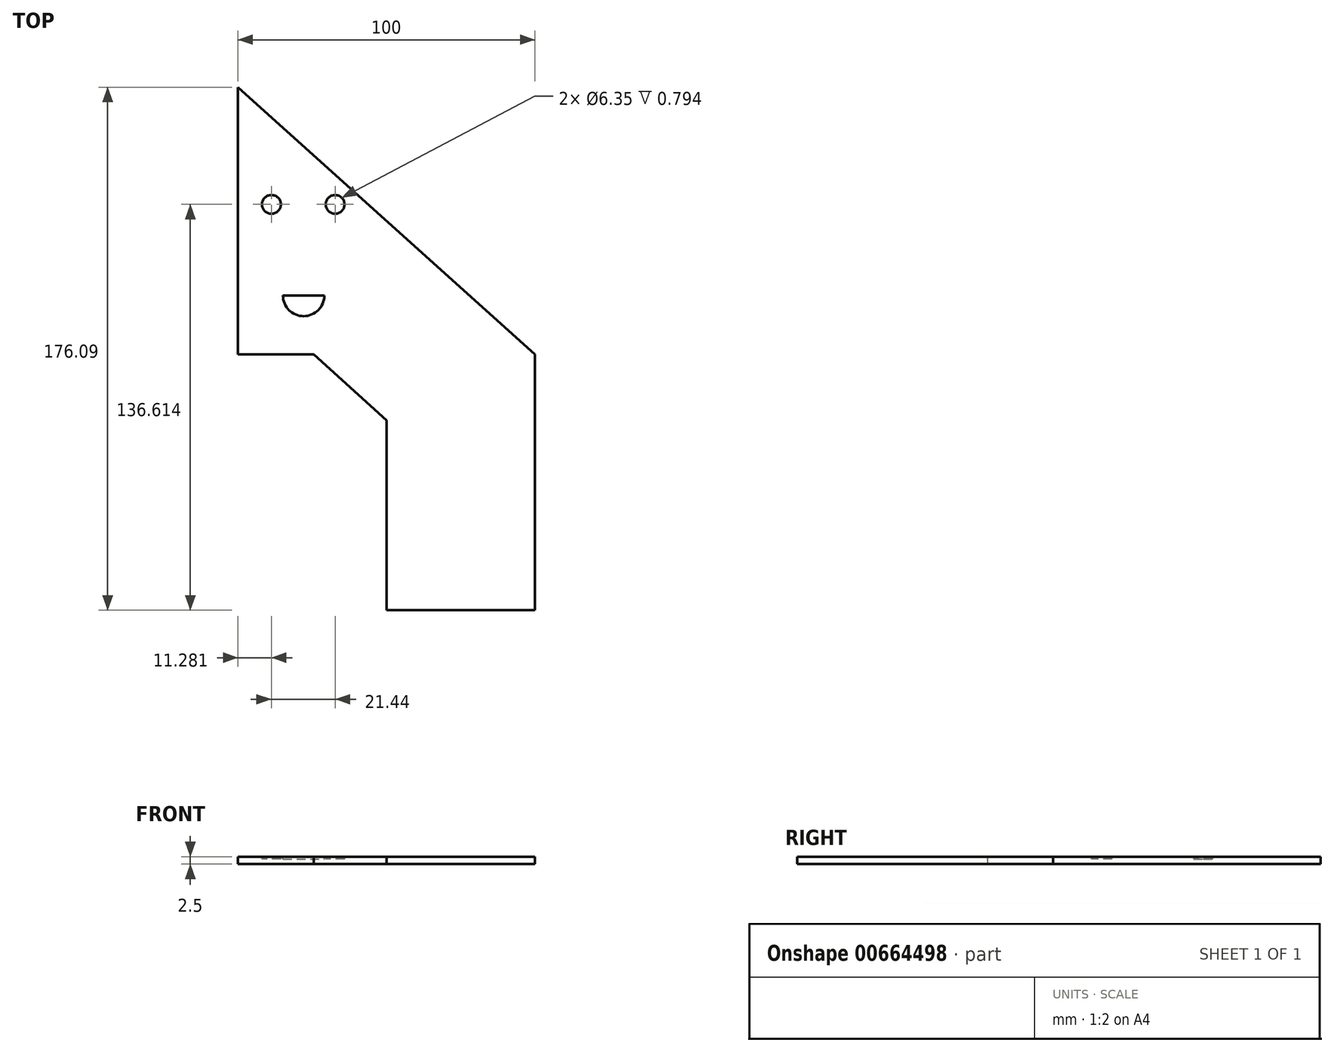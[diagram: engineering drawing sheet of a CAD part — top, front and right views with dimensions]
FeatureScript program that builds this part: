
annotation { "Feature Type Name" : "Feature", "Feature Type Description" : "" }
export const myFeature = defineFeature(function(context is Context, id is Id, definition is map)
    precondition{}
    {
        {
            var Q0;
            Q0=qCreatedBy(makeId("Top.planeOp"),FACE);
            var sketch = newSketch(context, id + "F0", { "sketchPlane" : qUnion([Q0])});
            skLineSegment(sketch, "E0", {"start": v(0, 0) * mm, "end": v(0, 90) * mm});
            skLineSegment(sketch, "E1", {"start": v(0, 0) * mm, "end": v(25.57, 0) * mm});
            skLineSegment(sketch, "E2", {"start": v(50, -22.15) * mm, "end": v(50, -86.1) * mm});
            skLineSegment(sketch, "E3", {"start": v(100, -86.1) * mm, "end": v(50, -86.1) * mm});
            skLineSegment(sketch, "E4", {"start": v(25.57, 0) * mm, "end": v(50, -22.15) * mm});
            skPoint(sketch, "E5.orphan", {"position": v(50, 0) * mm});
            skLineSegment(sketch, "E6", {"start": v(100, -86.1) * mm, "end": v(100, 0) * mm});
            skLineSegment(sketch, "E7", {"start": v(100, 0) * mm, "end": v(0, 90) * mm});
            skSolve(sketch);
        }
        {
            var Q0;
            Q0 = qSketchRegion(id + "F0", true);
            extrude(context, id + "F1", {"entities" : qUnion([Q0]), "depth" : 2.5 * mm, "offsetDistance" : 25.4 * mm});
        }
        {
            var Q0;
            Q0=makeQuery(id+"F1.opExtrude","CAP_FACE",FACE,{"disambiguationData":[OSD([sQuery(id+"F0.wireOp",EDGE,"E0"),sQuery(id+"F0.wireOp",EDGE,"E1"),sQuery(id+"F0.wireOp",EDGE,"VYQYnrsa-zGOh-645o-8oMv-SybQaaJVhyBb")])],"isStart":false});
            var sketch = newSketch(context, id + "F2", { "sketchPlane" : qUnion([Q0])});
            skLineSegment(sketch, "E8", {"start": v(0, 0) * mm, "end": v(0, 50.52) * mm});
            skSolve(sketch);
        }
        {
            var Q0;
            {var subQ0=sQuery(id+"F2.wireOp",EDGE,"E8");Q0=makeQuery(id+"F2.imprint","IMPRINT",FACE,{"disambiguationData":[TD([[makeQuery(id+"F2.imprint","IMPRINT",EDGE,{"derivedFrom":subQ0}),-1.0]])]});}
            var sketch = newSketch(context, id + "F3", { "sketchPlane" : qUnion([Q0])});
            skLineSegment(sketch, "E9.0", {"start": v(0, 0) * mm, "end": v(0, 0) * mm});
            skLineSegment(sketch, "E10.0.0", {"start": v(127, 0) * mm, "end": v(0, 127) * mm});
            skLineSegment(sketch, "E10.0.1", {"start": v(0, 127) * mm, "end": v(0, 50.52) * mm});
            skLineSegment(sketch, "E10.0.2", {"start": v(0, 50.52) * mm, "end": v(0, 0) * mm});
            skLineSegment(sketch, "E10.0.3", {"start": v(0, 0) * mm, "end": v(127, 0) * mm});
            skCircle(sketch, "E11", {"center": v(11.28, 50.52) * mm, "radius": 3.18 * mm});
            skCircle(sketch, "E12", {"center": v(32.72, 50.52) * mm, "radius": 3.18 * mm});
            skLineSegment(sketch, "E13", {"start": v(15.17, 19.85) * mm, "end": v(29.08, 19.85) * mm});
            skPoint(sketch, "E14.orphan", {"position": v(11.28, 19.85) * mm});
            skPoint(sketch, "E15.orphan", {"position": v(32.72, 19.85) * mm});
            skPoint(sketch, "E16.orphan", {"position": v(4.63, 19.85) * mm});
            skPoint(sketch, "E17.orphan", {"position": v(39.62, 19.85) * mm});
            skArc(sketch, "E18.trimOffspring", {"start": v(15.17, 19.85) * mm, "mid": v(22.12, 12.89) * mm, "end": v(29.08, 19.85) * mm});
            skSolve(sketch);
        }
        {
            var Q0;
            Q0=makeQuery(id+"F3.imprint","IMPRINT",FACE,{"disambiguationData":[TD([[makeQuery(id+"F3.imprint","IMPRINT",EDGE,{"derivedFrom":sQuery(id+"F3.wireOp",EDGE,"E13")}),-1.0]])]});
            var Q1;
            Q1=makeQuery(id+"F3.imprint","IMPRINT",FACE,{"disambiguationData":[TD([[makeQuery(id+"F3.imprint","IMPRINT",EDGE,{"derivedFrom":sQuery(id+"F3.wireOp",EDGE,"E11")}),1.0]])]});
            var Q2;
            Q2=makeQuery(id+"F3.imprint","IMPRINT",FACE,{"disambiguationData":[TD([[makeQuery(id+"F3.imprint","IMPRINT",EDGE,{"derivedFrom":sQuery(id+"F3.wireOp",EDGE,"E12")}),1.0]])]});
            extrude(context, id + "F4", {"entities" : qUnion([Q0, Q1, Q2]), "operationType" : NewBodyOperationType.REMOVE, "oppositeDirection" : true, "depth" : 0.8 * mm, "offsetDistance" : 25.4 * mm});
        }
    });
